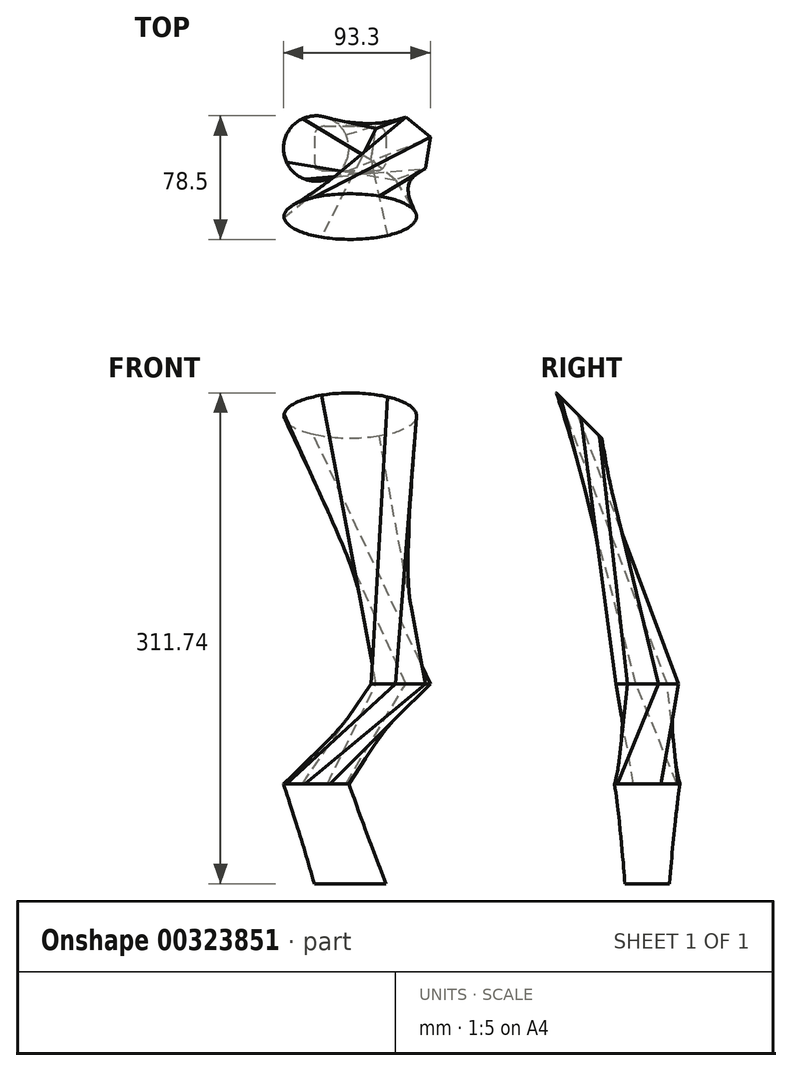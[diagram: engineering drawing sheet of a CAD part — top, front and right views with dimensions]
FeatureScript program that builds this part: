
annotation { "Feature Type Name" : "Feature", "Feature Type Description" : "" }
export const myFeature = defineFeature(function(context is Context, id is Id, definition is map)
    precondition{}
    {
        {
            var Q0;
            Q0=qCreatedBy(makeId("Front.planeOp"),FACE);
            var sketch = newSketch(context, id + "F0", { "sketchPlane" : qUnion([Q0])});
            skLineSegment(sketch, "E0.bottom", {"start": v(-162.17, 254) * mm, "end": v(162.17, 254) * mm});
            skLineSegment(sketch, "E0.top", {"start": v(-162.17, 0) * mm, "end": v(162.17, 0) * mm});
            skLineSegment(sketch, "E0.left", {"start": v(-162.17, 254) * mm, "end": v(-162.17, 0) * mm});
            skLineSegment(sketch, "E0.right", {"start": v(162.17, 254) * mm, "end": v(162.17, 0) * mm});
            skLineSegment(sketch, "E1", {"start": v(0, 0) * mm, "end": v(0, 288.66) * mm, "construction": true});
            skSolve(sketch);
        }
        {
            var Q0;
            Q0=sQuery(id+"F0.wireOp",EDGE,"E0.bottom");
            cPlane(context, id + "F1", {"entities" : qUnion([Q0]), "cplaneType" : CPlaneType.LINE_ANGLE, "offset" : 25.4 * mm, "angle" : 45 * degree, "width" : 152.4 * mm, "height" : 152.4 * mm});
        }
        {
            var Q0;
            Q0=qCreatedBy(id+"F1.planeOp",FACE);
            var sketch = newSketch(context, id + "F2", { "sketchPlane" : qUnion([Q0])});
            skEllipse(sketch, "E2", {"center": v(0, 240.76) * mm, "majorRadius": 42.1 * mm, "minorRadius": 20.5 * mm, "majorAxis": v(1, 0)});
            skSolve(sketch);
        }
        {
            var Q0;
            Q0=qCreatedBy(makeId("Top.planeOp"),FACE);
            var sketch = newSketch(context, id + "F3", { "sketchPlane" : qUnion([Q0])});
            skLineSegment(sketch, "E3.bottom", {"start": v(-16.46, 14.12) * mm, "end": v(16.46, 14.12) * mm});
            skLineSegment(sketch, "E3.top", {"start": v(-16.46, -14.12) * mm, "end": v(16.46, -14.12) * mm});
            skLineSegment(sketch, "E3.left", {"start": v(-22.81, 7.77) * mm, "end": v(-22.81, -7.77) * mm});
            skLineSegment(sketch, "E3.right", {"start": v(22.81, 7.77) * mm, "end": v(22.81, -7.77) * mm});
            skPoint(sketch, "E4.visualSharp", {"position": v(22.81, 14.12) * mm});
            skArc(sketch, "E4.filletArc", {"start": v(22.81, 7.77) * mm, "mid": v(20.95, 12.26) * mm, "end": v(16.46, 14.12) * mm});
            skPoint(sketch, "E5.visualSharp", {"position": v(22.81, -14.12) * mm});
            skArc(sketch, "E5.filletArc", {"start": v(16.46, -14.12) * mm, "mid": v(20.95, -12.26) * mm, "end": v(22.81, -7.77) * mm});
            skPoint(sketch, "E6.visualSharp", {"position": v(-22.81, -14.12) * mm});
            skArc(sketch, "E6.filletArc", {"start": v(-22.81, -7.77) * mm, "mid": v(-20.95, -12.26) * mm, "end": v(-16.46, -14.12) * mm});
            skPoint(sketch, "E7.visualSharp", {"position": v(-22.81, 14.12) * mm});
            skArc(sketch, "E7.filletArc", {"start": v(-16.46, 14.12) * mm, "mid": v(-20.95, 12.26) * mm, "end": v(-22.81, 7.77) * mm});
            skSolve(sketch);
        }
        {
            var Q0;
            Q0=qCreatedBy(makeId("Top.planeOp"),FACE);
            cPlane(context, id + "F4", {"entities" : qUnion([Q0]), "cplaneType" : CPlaneType.OFFSET, "offset" : 127 * mm, "width" : 152.4 * mm, "height" : 152.4 * mm});
        }
        {
            var Q0;
            Q0=qCreatedBy(makeId("Top.planeOp"),FACE);
            cPlane(context, id + "F5", {"entities" : qUnion([Q0]), "cplaneType" : CPlaneType.OFFSET, "offset" : 63.5 * mm, "width" : 152.4 * mm, "height" : 152.4 * mm});
        }
        {
            var Q0;
            Q0=qCreatedBy(id+"F5.planeOp",FACE);
            var sketch = newSketch(context, id + "F6", { "sketchPlane" : qUnion([Q0])});
            skCircle(sketch, "E8", {"center": v(-21.66, 0) * mm, "radius": 20.76 * mm});
            skSolve(sketch);
        }
        {
            var Q0;
            Q0=qCreatedBy(id+"F4.planeOp",FACE);
            var sketch = newSketch(context, id + "F7", { "sketchPlane" : qUnion([Q0])});
            skCircle(sketch, "E9.cCircle", {"center": v(32.04, 0) * mm, "radius": 17.46 * mm, "construction": true});
            skLineSegment(sketch, "E9.0", {"start": v(47.67, -12.73) * mm, "end": v(28.82, -19.9) * mm});
            skLineSegment(sketch, "E9.1", {"start": v(28.82, -19.9) * mm, "end": v(13.2, -7.17) * mm});
            skLineSegment(sketch, "E9.2", {"start": v(13.2, -7.17) * mm, "end": v(16.4, 12.73) * mm});
            skLineSegment(sketch, "E9.3", {"start": v(16.4, 12.73) * mm, "end": v(35.25, 19.9) * mm});
            skLineSegment(sketch, "E9.4", {"start": v(35.25, 19.9) * mm, "end": v(50.88, 7.17) * mm});
            skLineSegment(sketch, "E9.5", {"start": v(50.88, 7.17) * mm, "end": v(47.67, -12.73) * mm});
            skPoint(sketch, "E9.0.midPoint", {"position": v(38.25, -16.32) * mm});
            skSolve(sketch);
        }
        {
            var Q0;
            Q0=makeQuery(id+"F3.imprint","IMPRINT",FACE,{"disambiguationData":[TD([[makeQuery(id+"F3.imprint","IMPRINT",EDGE,{"derivedFrom":sQuery(id+"F3.wireOp",EDGE,"E3.bottom")}),-1.0]])]});
            var Q1;
            Q1=makeQuery(id+"F6.imprint","IMPRINT",FACE,{"disambiguationData":[TD([[makeQuery(id+"F6.imprint","IMPRINT",EDGE,{"derivedFrom":sQuery(id+"F6.wireOp",EDGE,"E8")}),1.0]])]});
            loft(context, id + "F8", {"sheetProfilesArray" : [{ "sheetProfileEntities" : qUnion([Q0]) }, { "sheetProfileEntities" : qUnion([Q1]) }]});
        }
        {
            var Q1;
            Q1=makeQuery(id+"F8.opLoft","CAP_FACE",FACE,{"disambiguationData":[OSD([makeQuery(id+"F6.imprint","IMPRINT",FACE,{"disambiguationData":[TD([[makeQuery(id+"F6.imprint","IMPRINT",EDGE,{"derivedFrom":sQuery(id+"F6.wireOp",EDGE,"E8")}),1.0]])]})])],"isStart":true});
            var Q2;
            Q2=makeQuery(id+"F7.imprint","IMPRINT",FACE,{"disambiguationData":[TD([[makeQuery(id+"F7.imprint","IMPRINT",EDGE,{"derivedFrom":sQuery(id+"F7.wireOp",EDGE,"E9.0")}),-1.0]])]});
            loft(context, id + "F9", {"operationType" : NewBodyOperationType.ADD, "sheetProfilesArray" : [{ "sheetProfileEntities" : qUnion([Q1]) }, { "sheetProfileEntities" : qUnion([Q2]) }]});
        }
        {
            var Q0;
            Q0=sQuery(id+"F2.wireOp",VERTEX,"E2.center");
            var Q1;
            Q1=makeQuery(id+"F9.opLoft","MID_CAP_VERTEX",VERTEX,{"disambiguationData":[OSD([sQuery(id+"F7.wireOp",EDGE,"E9.4"),sQuery(id+"F7.wireOp",EDGE,"E9.5")])],"capPos":1.0});
            var Q2;
            Q2=makeQuery(id+"F9.opLoft","MID_CAP_VERTEX",VERTEX,{"disambiguationData":[OSD([sQuery(id+"F7.wireOp",EDGE,"E9.1"),sQuery(id+"F7.wireOp",EDGE,"E9.2")])],"capPos":1.0});
            cPlane(context, id + "F10", {"entities" : qUnion([Q0, Q1, Q2]), "cplaneType" : CPlaneType.THREE_POINT, "offset" : 25.4 * mm, "width" : 152.4 * mm, "height" : 152.4 * mm});
        }
        {
            var Q1;
            Q1=makeQuery(id+"F9.opLoft","CAP_FACE",FACE,{"disambiguationData":[OSD([makeQuery(id+"F7.imprint","IMPRINT",FACE,{"disambiguationData":[TD([[makeQuery(id+"F7.imprint","IMPRINT",EDGE,{"derivedFrom":sQuery(id+"F7.wireOp",EDGE,"E9.0")}),-1.0]])]})])],"isStart":true});
            var Q2;
            Q2=makeQuery(id+"F2.imprint","IMPRINT",FACE,{"disambiguationData":[TD([[makeQuery(id+"F2.imprint","IMPRINT",EDGE,{"derivedFrom":sQuery(id+"F2.wireOp",EDGE,"E2")}),1.0]])]});
            loft(context, id + "F11", {"operationType" : NewBodyOperationType.ADD, "sheetProfilesArray" : [{ "sheetProfileEntities" : qUnion([Q1]) }, { "sheetProfileEntities" : qUnion([Q2]) }]});
        }
    });
